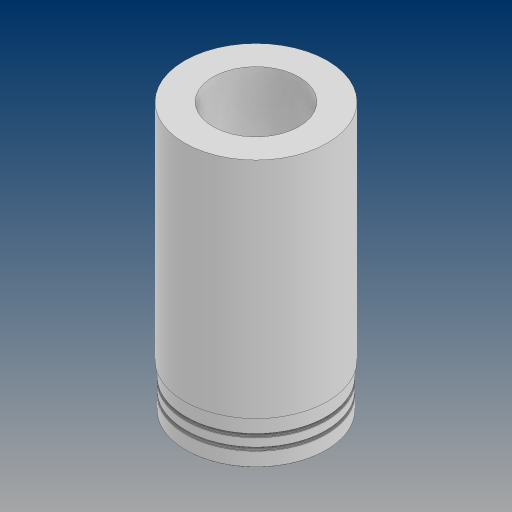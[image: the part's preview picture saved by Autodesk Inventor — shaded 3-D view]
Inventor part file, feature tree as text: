
AUTODESK INVENTOR PART (.ipt)
format: ipt  version: 2024.3 (Build 283343000, 343)  size: 352,768 bytes
history: native  units: in
note: dims shown in document units (in); Inventor stores cm internally (conversion verified against a paired STEP export)
features: fillet x3, other x2, extrude x1, sketch x1, revolve x1
ambient origin geometry x8: Origin, YZ Plane, XZ Plane, XY Plane, X Axis, Y Axis, Z Axis, Center Point
bodies: Solid1 (feature_tree), Solid2 (feature_tree), Solid3 (feature_tree), Solid4 (feature_tree), Solid5 (feature_tree), Solid6 (feature_tree)
feature tree (8):
  extrude  "Extrusion1"  [1 undecoded]
  sketch  "Sketch1"  dims[d0=1.0in d1=0.0in]
  revolve  "Revolve2"  [1 undecoded]
  other  "CirPattern1[1]"
  other  "CirPattern1[2]"
  fillet  "Fillet2"  [1 undecoded]
  fillet  "Fillet1"  [1 undecoded]
  fillet  "Fillet3"  [1 undecoded]
note: 5 required parameter values undecoded (feature->parameter linkage not recoverable at this tier; creation-order binding heuristic only, values carry confidence <= 0.55)
